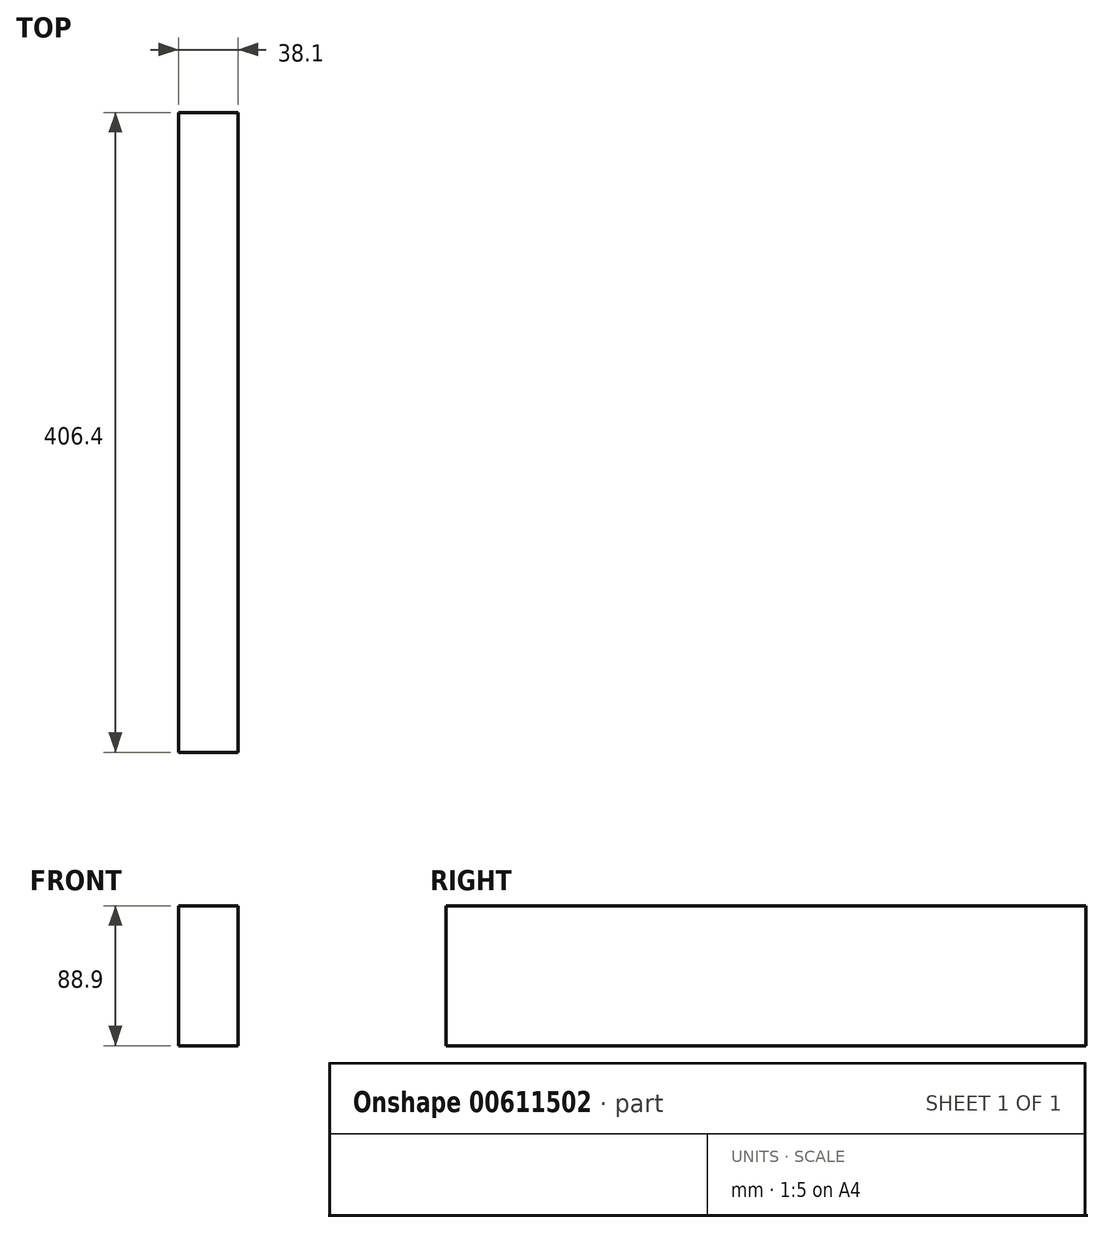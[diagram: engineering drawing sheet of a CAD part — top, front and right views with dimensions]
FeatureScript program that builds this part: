
annotation { "Feature Type Name" : "Feature", "Feature Type Description" : "" }
export const myFeature = defineFeature(function(context is Context, id is Id, definition is map)
    precondition{}
    {
        {
            var Q0;
            Q0=qCreatedBy(makeId("Front.planeOp"),FACE);
            var sketch = newSketch(context, id + "F0", { "sketchPlane" : qUnion([Q0])});
            skLineSegment(sketch, "E0.bottom", {"start": v(-16.29, 88.9) * mm, "end": v(21.81, 88.9) * mm});
            skLineSegment(sketch, "E0.top", {"start": v(-16.29, 0) * mm, "end": v(21.81, 0) * mm});
            skLineSegment(sketch, "E0.left", {"start": v(-16.29, 88.9) * mm, "end": v(-16.29, 0) * mm});
            skLineSegment(sketch, "E0.right", {"start": v(21.81, 88.9) * mm, "end": v(21.81, 0) * mm});
            skSolve(sketch);
        }
        {
            var Q0;
            Q0 = qSketchRegion(id + "F0", true);
            var Q1;
            Q1=makeQuery(id+"F0.imprint","IMPRINT",FACE,{"disambiguationData":[TD([[makeQuery(id+"F0.imprint","IMPRINT",EDGE,{"derivedFrom":sQuery(id+"F0.wireOp",EDGE,"E0.bottom")}),-1.0]])]});
            extrude(context, id + "F1", {"entities" : qUnion([Q0, Q1]), "depth" : 406.4 * mm, "offsetDistance" : 25.4 * mm});
        }
    });
